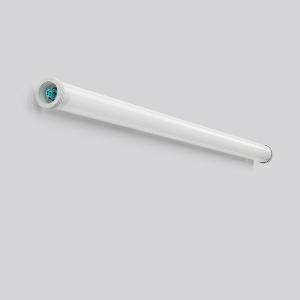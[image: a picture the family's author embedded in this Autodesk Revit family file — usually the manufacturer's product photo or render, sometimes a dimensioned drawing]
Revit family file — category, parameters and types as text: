
# Revit family: planox_tube_601072_002_76_deaf
name_source: partatom
category: Lighting Fixtures
units: mm (PartAtom-declared; Revit-internal decimal feet)

## family parameters
Cut with Voids When Loaded = No
Host = Face
Light Source = No
Part Type = Normal
Room Calculation Point = No
Round Connector Dimension = Use Diameter
Shared = No

## types (1)
- PLANOX TUBE (1 x LED Modul 840, 8650 lm, 4000)
    Apparent Load = 62 VA
    CIE Flux Codes = 42 71 90 91 100
    Color Rendering = 80
    Color Temperature = 4000
    Default Elevation = 1800 mm
    Description = Series: PLANOX TUBE
Robust protective tube luminaire for tough requirements. Rack made of sheet steel, white powder coated. End caps made of plastic (polyamide) grey. Diffuser made of plastic (polycarbonate), opal, shockproof. Symmetrical light distribution. Homogeneous light distribution. With accessories for wall, ceiling or pendant mounting. Driver integrated.Easy installation with the Plug+Play Wieland RST CLASSIC plug-in system. Mounting set must be ordered separately. Luminaire with limited surface temperature in accordance with EN 60598-2-24 for use in environments in which a deposit of conductive dust on the luminaire can be expected. Qualified for use in the food and drink industry. Suitable for lighting in public car parks and public off-street parking spaces according to DIN 67528. Environmentally friendly and resource-saving due to replaceable components. 
Colour: white
Diameter: 78 mm
Length: 1564 mm
Lamp: LED
Socket: without socket
Colour temperature: 4000K
Colour rendering index (CRI): 83
System power: 62 W
Rated luminous flux: 8650 lm
Luminous efficiency: 140 lm/W
Control gear: Converter, dimmable, DALI
Protection class: I
Type of protection: IP 67
    Height = 0 mm  [stored 0 ft]
    Lamp = 1 x LED Modul 840
    Lamp Light Flux = 8650 lm
    Lamp count = 1
    Length = 1564 mm
    Lifetime = 50000 h
    Luminous efficacy = 140 lm/W
    Manufacturer = RZB
    ModVariant = No
    Model = 601072.002.76
    Mounting Place = Ceiling
    Mounting Type = Surface mounted
    Number of Poles = 1
    OnlyDefault = Yes
    Power Factor = 1
    Product Name = PLANOX TUBE
    Product group = Surface mounted luminaires for moist/humid enviroments
    ProductGroupID = 308
    Protection Class = Protection class I
    Protection Degree = Degree of protection
    RLX_Detail_Level = 1
    RLX_Emergency_Light_Flux = 0 lm
    RLX_Emergency_Type = 0
    RLX_Emergency_Type_DB = No
    RlxData = <blob elided: 34909 chars, md5=3f7a658c>
    Socket = socket
    Standby Power = 0 W
    System Light Flux = 8650 lm
    System Power = 62 W
    Type Comments = Product without accessories
    Type Image = 601072.002.76.jpg
    URL = http://relux.com
    VarID = ---
    Voltage = 0 V
    Weight = 0.00 kg
    Width = 0 mm  [stored 0 ft]

note: [stored X ft] marks values corroborated as IEEE doubles in the binary element streams (Revit-internal decimal feet)

## geometry (parser evidence)
native form markers: Blend x4, Sweep x11
no freeform markers — native parametric forms only
